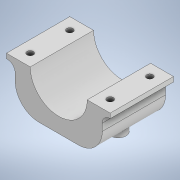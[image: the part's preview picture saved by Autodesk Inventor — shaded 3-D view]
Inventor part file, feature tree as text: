
AUTODESK INVENTOR PART (.ipt)
format: ipt  version: 2021 (Build 250183000, 183)  size: 179,200 bytes
history: native  units: mm
features: extrude x4, sketch x4
ambient origin geometry x8: Origin, YZ Plane, XZ Plane, XY Plane, X Axis, Y Axis, Z Axis, Center Point
bodies: Solid1 (feature_tree)
feature tree (8):
  extrude  "Extrusion1"  Depth=55.0mm
  extrude  "Extrusion2"  Depth=3.0mm
  extrude  "Extrusion3"  Depth=5.0mm
  extrude  "Extrusion4"  TaperAngle=90.0deg  [1 undecoded]
  sketch  "Sketch1"  dims[d0=36.0mm d1=55.0mm]
  sketch  "Sketch2"  dims[d2=15.0mm d3=3.0mm]
  sketch  "Sketch3"  dims[d4=5.0mm d5=5.0mm]
  sketch  "Sketch4"  dims[d6=3.0mm d7=90.0deg d8=5.0mm d9=40.0mm d10=0.0mm d11=15.0mm d12=10.0mm d13=10.0mm d14=5.0mm d15=0.0mm d16=4.0mm d17=4.0mm d18=15.0mm d19=0.0mm d20=4.0mm d21=7.5mm d22=7.5mm d23=20.0mm d25=50.5mm d26=20.0mm d28=25.0mm d31=10.0mm d32=0.0mm]
note: 1 required parameter value undecoded (feature->parameter linkage not recoverable at this tier; creation-order binding heuristic only, values carry confidence <= 0.55)
